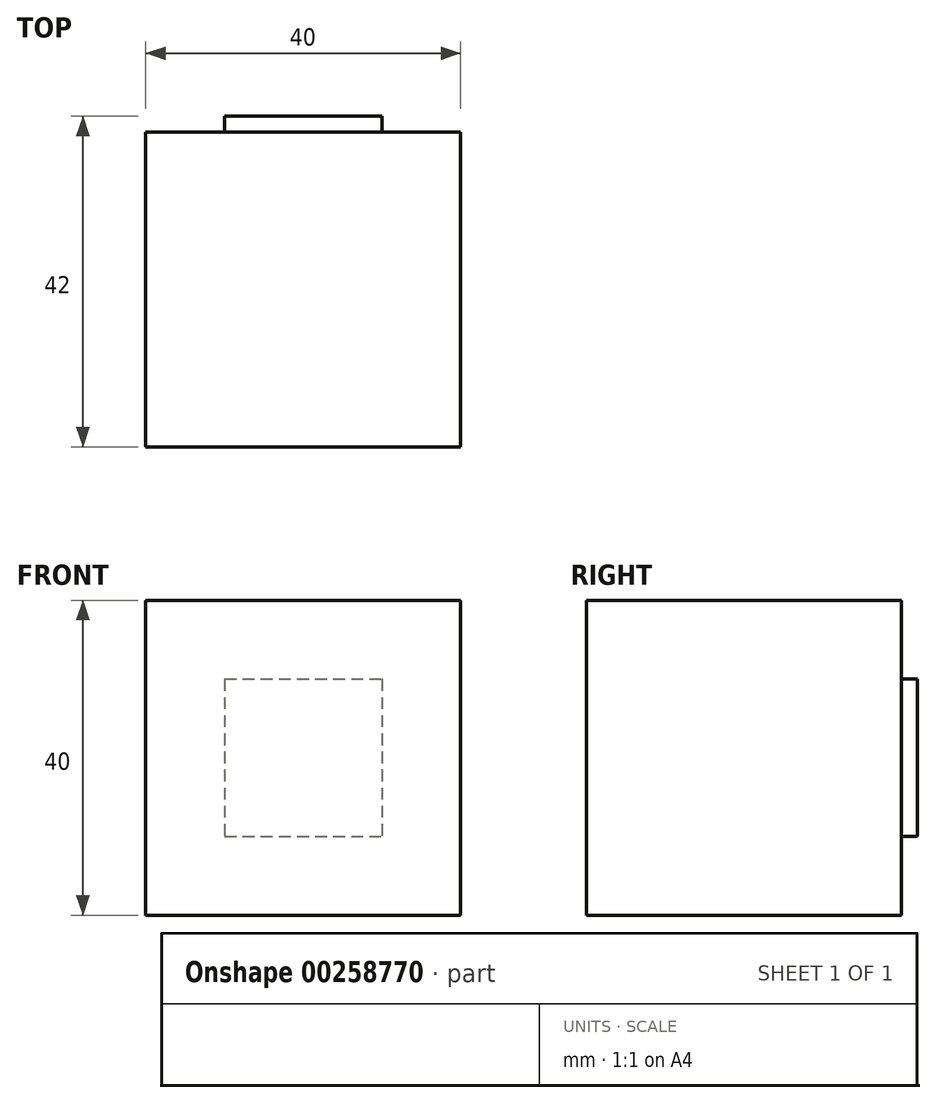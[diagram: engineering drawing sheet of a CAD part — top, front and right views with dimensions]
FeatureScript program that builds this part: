
annotation { "Feature Type Name" : "Feature", "Feature Type Description" : "" }
export const myFeature = defineFeature(function(context is Context, id is Id, definition is map)
    precondition{}
    {
        {
            var Q0;
            Q0=qCreatedBy(makeId("Front.planeOp"),FACE);
            var sketch = newSketch(context, id + "F0", { "sketchPlane" : qUnion([Q0])});
            skLineSegment(sketch, "E0.bottom", {"start": v(20, -20) * mm, "end": v(-20, -20) * mm});
            skLineSegment(sketch, "E0.top", {"start": v(20, 20) * mm, "end": v(-20, 20) * mm});
            skLineSegment(sketch, "E0.left", {"start": v(20, -20) * mm, "end": v(20, 20) * mm});
            skLineSegment(sketch, "E0.right", {"start": v(-20, -20) * mm, "end": v(-20, 20) * mm});
            skPoint(sketch, "E0.middle", {"position": v(0, 0) * mm});
            skSolve(sketch);
        }
        {
            var Q0;
            Q0=makeQuery(id+"F0.imprint","IMPRINT",FACE,{"disambiguationData":[TD([[makeQuery(id+"F0.imprint","IMPRINT",EDGE,{"derivedFrom":sQuery(id+"F0.wireOp",EDGE,"E0.bottom")}),-1.0]])]});
            extrude(context, id + "F1", {"entities" : qUnion([Q0]), "depth" : 40 * mm});
        }
        {
            var Q0;
            Q0=qCreatedBy(makeId("Front.planeOp"),FACE);
            var sketch = newSketch(context, id + "F2", { "sketchPlane" : qUnion([Q0])});
            skLineSegment(sketch, "E1.bottom", {"start": v(-10, 10) * mm, "end": v(10, 10) * mm});
            skLineSegment(sketch, "E1.top", {"start": v(-10, -10) * mm, "end": v(10, -10) * mm});
            skLineSegment(sketch, "E1.left", {"start": v(-10, 10) * mm, "end": v(-10, -10) * mm});
            skLineSegment(sketch, "E1.right", {"start": v(10, 10) * mm, "end": v(10, -10) * mm});
            skPoint(sketch, "E1.middle", {"position": v(0, 0) * mm});
            skSolve(sketch);
        }
        {
            var Q0;
            Q0=makeQuery(id+"F2.imprint","IMPRINT",FACE,{"disambiguationData":[TD([[makeQuery(id+"F2.imprint","IMPRINT",EDGE,{"derivedFrom":sQuery(id+"F2.wireOp",EDGE,"E1.bottom")}),-1.0]])]});
            extrude(context, id + "F3", {"entities" : qUnion([Q0]), "operationType" : NewBodyOperationType.ADD, "oppositeDirection" : true, "depth" : 2 * mm});
        }
    });
